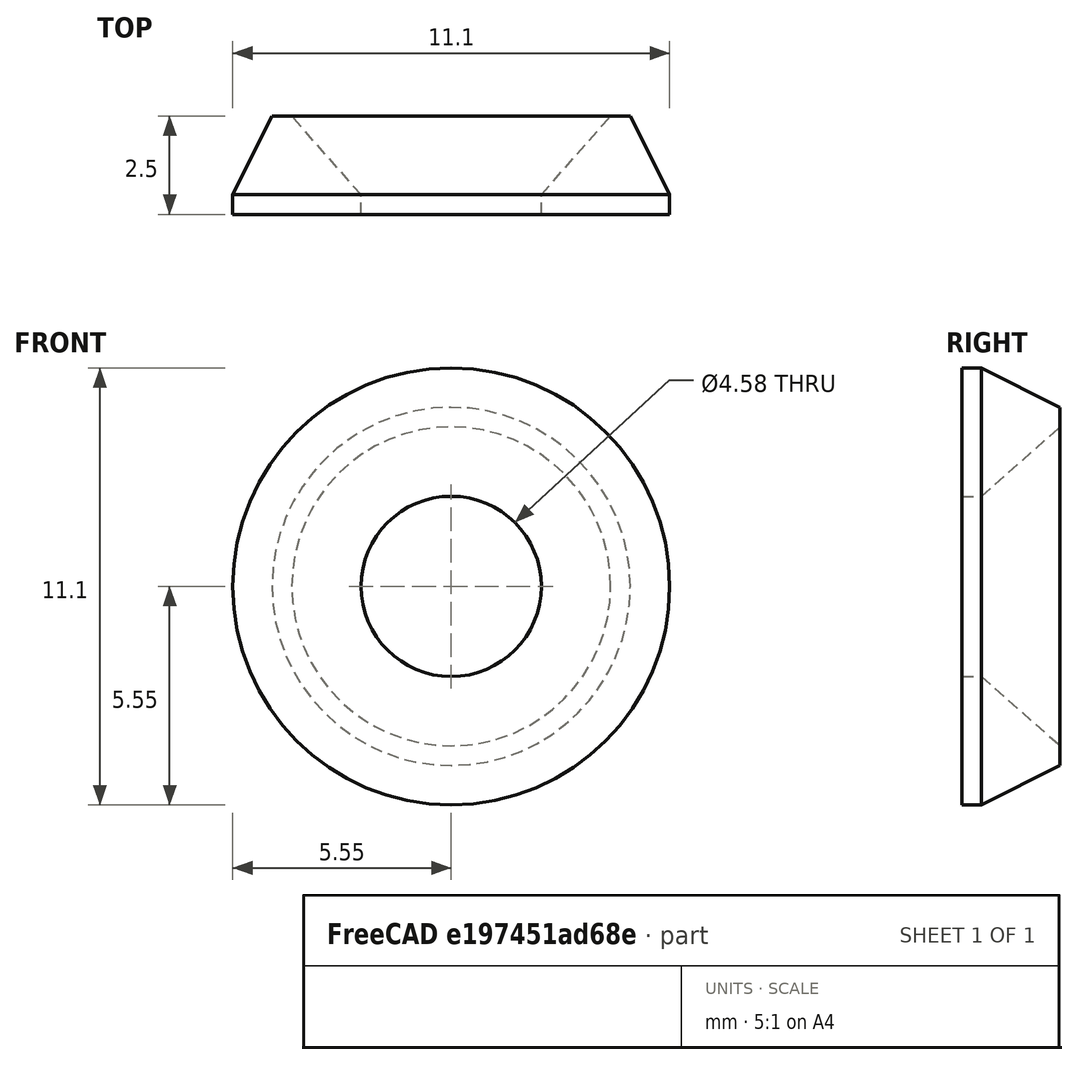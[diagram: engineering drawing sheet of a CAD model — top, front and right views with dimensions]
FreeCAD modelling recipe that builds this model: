
FCSTD DOCUMENT  (FreeCAD 0.18.3R)
Label: led_reflector
License: All rights reserved
LicenseURL: http://en.wikipedia.org/wiki/All_rights_reserved
objects: Sketcher::SketchObject×1, PartDesign::Revolution×1, PartDesign::Body×1
note: 4 computed .brp shape members not serialized (recipe doc carries the construction recipe); baked Part::Feature solids carry a one-line shape summary decoded from their .brp

FEATURE [Sketcher::SketchObject] Sketch
  MapMode = 5
  Support = -> [XY_Plane]
  sketch-geometry (9):
    g0: LineSegment [constr] StartX=0 StartY=0 StartZ=0 EndX=2.29 EndY=0 EndZ=0
    g1: LineSegment StartX=2.29 StartY=0 StartZ=0 EndX=5.55 EndY=0 EndZ=0
    g2: LineSegment StartX=5.55 StartY=0 StartZ=0 EndX=5.55 EndY=0.5 EndZ=0
    g3: LineSegment [constr] StartX=5.55 StartY=0.5 StartZ=0 EndX=4.55 EndY=0.5 EndZ=0
    g4: LineSegment [constr] StartX=4.55 StartY=0.5 StartZ=0 EndX=4.55 EndY=2.5 EndZ=0
    g5: LineSegment StartX=4.55 StartY=2.5 StartZ=0 EndX=5.55 EndY=0.5 EndZ=0
    g6: LineSegment StartX=4.55 StartY=2.5 StartZ=0 EndX=4.05 EndY=2.5 EndZ=0
    g7: LineSegment StartX=2.29 StartY=0 StartZ=0 EndX=2.29 EndY=0.5 EndZ=0
    g8: LineSegment StartX=2.29 StartY=0.5 StartZ=0 EndX=4.05 EndY=2.5 EndZ=0
  constraints (25):
    c: Coincident(g0,g-1)
    c: Horizontal(g0)
    c: DistanceX(g0,g0) = 2.29
    c: Coincident(g1,g0)
    c: Horizontal(g1)
    c: DistanceX(g1,g1) = 3.26
    c: Coincident(g2,g1)
    c: Vertical(g2)
    c: DistanceY(g2,g2) = 0.5
    c: Coincident(g3,g2)
    c: Horizontal(g3)
    c: Coincident(g4,g3)
    c: Perpendicular(g3,g4)
    c: Coincident(g5,g4)
    c: Coincident(g5,g2)
    c: DistanceY(g4,g4) = 2
    c: DistanceX(g3,g3) = 1
    c: Coincident(g6,g5)
    c: Horizontal(g6)
    c: DistanceX(g6,g6) = 0.5
    c: Coincident(g7,g1)
    c: Vertical(g7)
    c: Equal(g7,g2)
    c: Coincident(g8,g7)
    c: Coincident(g8,g6)
FEATURE [PartDesign::Revolution] Revolution
  Angle = 360
  Axis = (0,1,0)
  Base = (0,0,0)
  Profile = -> Sketch
  ReferenceAxis = -> Sketch [V_Axis]
  Reversed = true
FEATURE [PartDesign::Body] Body
  Group = -> [Sketch,Revolution]
  Origin = -> Origin
  Tip = -> Revolution
